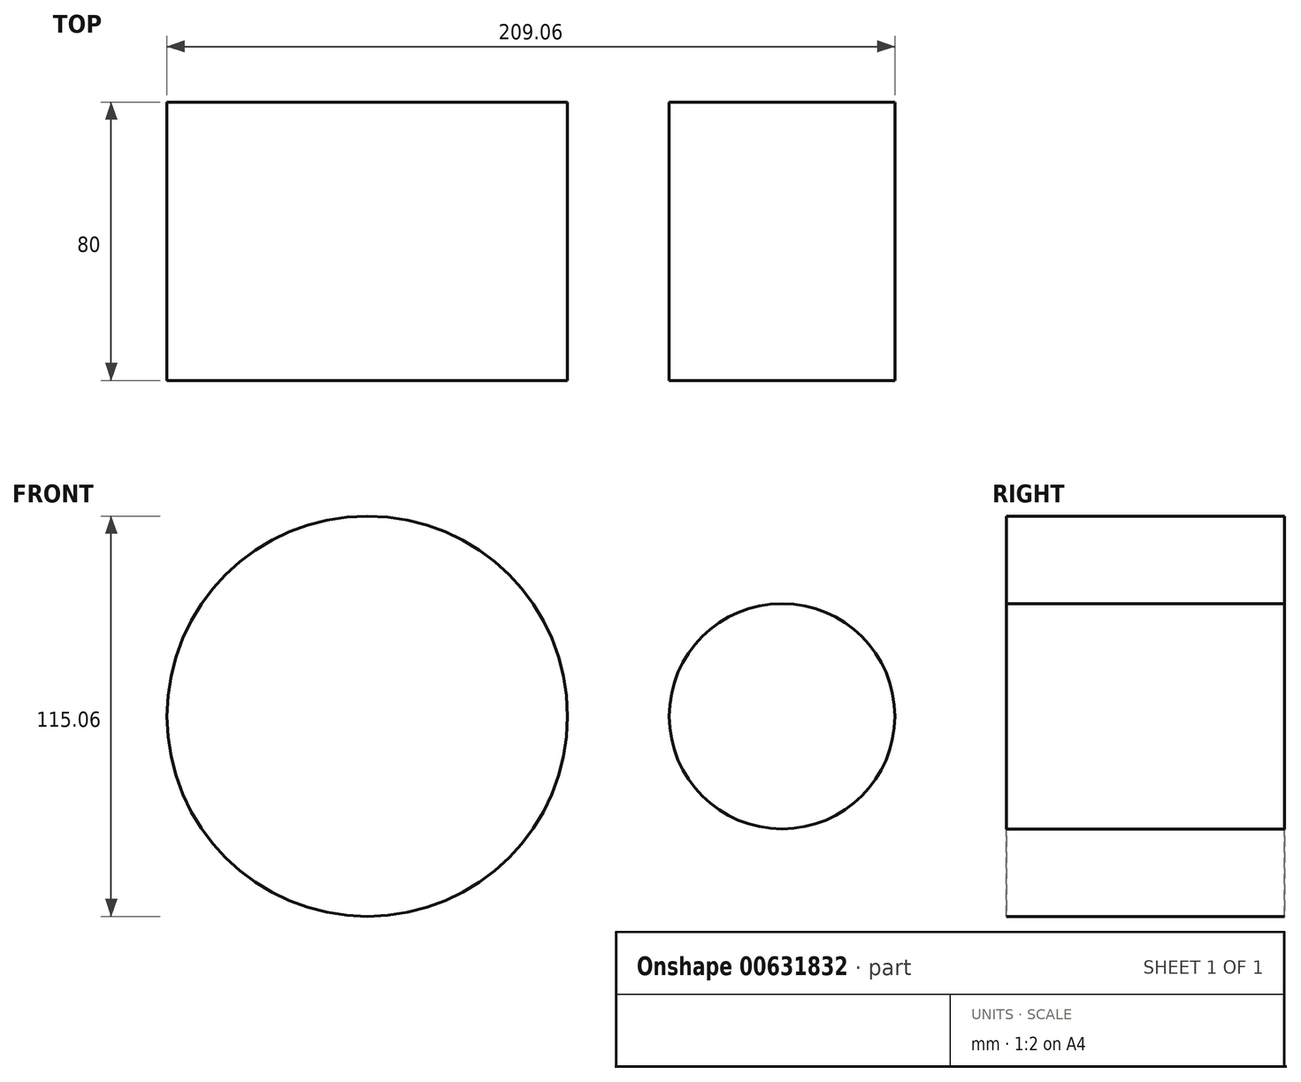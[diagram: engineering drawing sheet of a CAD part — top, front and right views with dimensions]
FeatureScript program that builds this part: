
annotation { "Feature Type Name" : "Feature", "Feature Type Description" : "" }
export const myFeature = defineFeature(function(context is Context, id is Id, definition is map)
    precondition{}
    {
        {
            var Q0;
            Q0=qCreatedBy(makeId("Front.planeOp"),FACE);
            var sketch = newSketch(context, id + "F0", { "sketchPlane" : qUnion([Q0])});
            skCircle(sketch, "E0", {"center": v(0, 0) * mm, "radius": 57.53 * mm});
            skCircle(sketch, "E1", {"center": v(119.13, 0) * mm, "radius": 32.4 * mm});
            skSolve(sketch);
        }
        {
            var Q0;
            Q0=makeQuery(id+"F0.imprint","IMPRINT",FACE,{"disambiguationData":[TD([[makeQuery(id+"F0.imprint","IMPRINT",EDGE,{"derivedFrom":sQuery(id+"F0.wireOp",EDGE,"E0")}),1.0]])]});
            var Q1;
            Q1=makeQuery(id+"F0.imprint","IMPRINT",FACE,{"disambiguationData":[TD([[makeQuery(id+"F0.imprint","IMPRINT",EDGE,{"derivedFrom":sQuery(id+"F0.wireOp",EDGE,"E1")}),1.0]])]});
            extrude(context, id + "F1", {"entities" : qUnion([Q0, Q1]), "oppositeDirection" : true, "depth" : 80 * mm, "offsetDistance" : 25 * mm});
        }
    });
